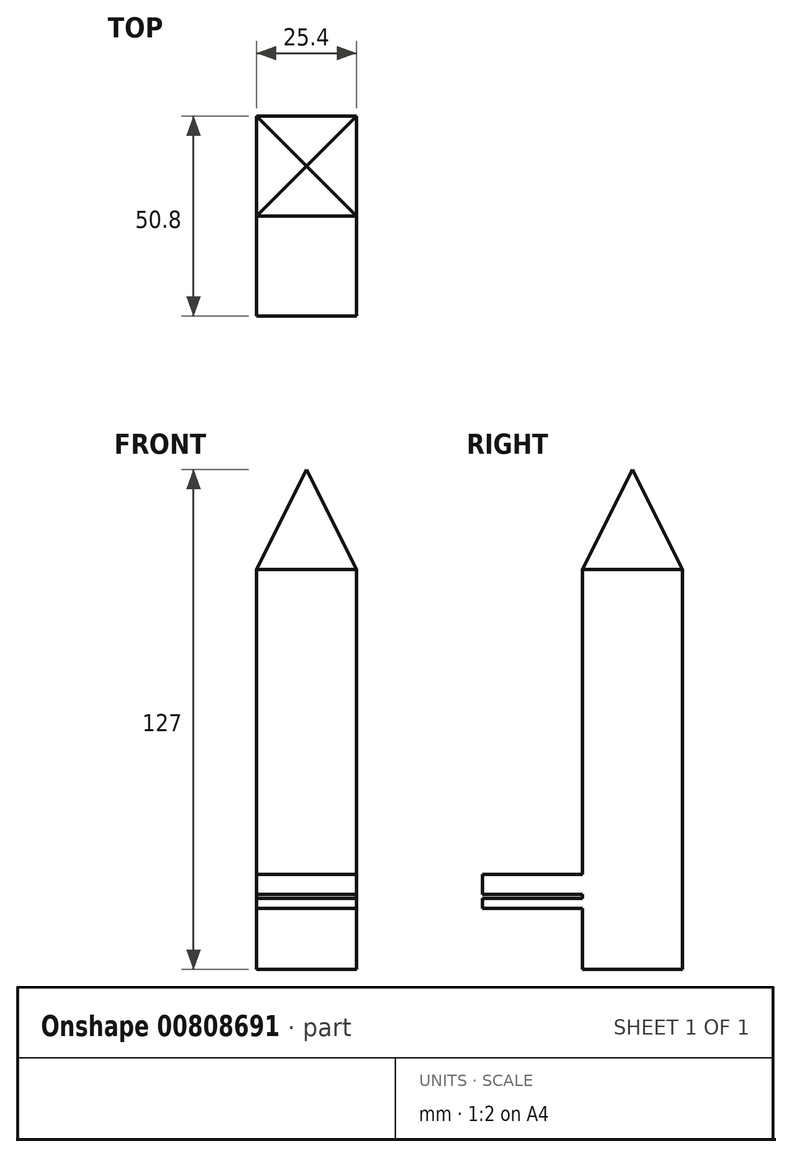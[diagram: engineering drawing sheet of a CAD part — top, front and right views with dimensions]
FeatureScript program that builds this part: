
annotation { "Feature Type Name" : "Feature", "Feature Type Description" : "" }
export const myFeature = defineFeature(function(context is Context, id is Id, definition is map)
    precondition{}
    {
        {
            var Q0;
            Q0=qCreatedBy(makeId("Top.planeOp"),FACE);
            var sketch = newSketch(context, id + "F0", { "sketchPlane" : qUnion([Q0])});
            skLineSegment(sketch, "E0.bottom", {"start": v(-11.7, 11.54) * mm, "end": v(13.7, 11.54) * mm});
            skLineSegment(sketch, "E0.top", {"start": v(-11.7, -13.86) * mm, "end": v(13.7, -13.86) * mm});
            skLineSegment(sketch, "E0.left", {"start": v(-11.7, 11.54) * mm, "end": v(-11.7, -13.86) * mm});
            skLineSegment(sketch, "E0.right", {"start": v(13.7, 11.54) * mm, "end": v(13.7, -13.86) * mm});
            skSolve(sketch);
        }
        {
            var Q0;
            Q0 = qSketchRegion(id + "F0", true);
            extrude(context, id + "F1", {"entities" : qUnion([Q0]), "depth" : 101.6 * mm, "offsetDistance" : 25.4 * mm});
        }
        {
            var Q0;
            Q0=makeQuery(id+"F1.opExtrude","CAP_FACE",FACE,{"disambiguationData":[OSD([sQuery(id+"F0.wireOp",EDGE,"E0.bottom"),sQuery(id+"F0.wireOp",EDGE,"E0.top"),sQuery(id+"F0.wireOp",EDGE,"E0.left"),sQuery(id+"F0.wireOp",EDGE,"E0.right")])],"isStart":false});
            cPlane(context, id + "F2", {"entities" : qUnion([Q0]), "cplaneType" : CPlaneType.OFFSET, "offset" : 25.4 * mm, "width" : 152.4 * mm, "height" : 152.4 * mm});
        }
        {
            var Q0;
            Q0=qCreatedBy(id+"F2.planeOp",FACE);
            var sketch = newSketch(context, id + "F3", { "sketchPlane" : qUnion([Q0])});
            skLineSegment(sketch, "E1.bottom", {"start": v(-11.7, 11.54) * mm, "end": v(13.7, 11.54) * mm, "construction": true});
            skLineSegment(sketch, "E1.top", {"start": v(-11.7, -13.86) * mm, "end": v(13.7, -13.86) * mm, "construction": true});
            skLineSegment(sketch, "E1.left", {"start": v(-11.7, 11.54) * mm, "end": v(-11.7, -13.86) * mm, "construction": true});
            skLineSegment(sketch, "E1.right", {"start": v(13.7, 11.54) * mm, "end": v(13.7, -13.86) * mm, "construction": true});
            skLineSegment(sketch, "E2", {"start": v(1, -13.86) * mm, "end": v(1, 11.54) * mm, "construction": true});
            skLineSegment(sketch, "E3", {"start": v(-11.7, -1.16) * mm, "end": v(13.7, -1.16) * mm, "construction": true});
            skPoint(sketch, "E4", {"position": v(1, -1.16) * mm});
            skSolve(sketch);
        }
        {
            var Q0;
            Q0=sQuery(id+"F3.wireOp",VERTEX,"E4");
            var Q1;
            Q1=makeQuery(id+"F1.opExtrude","CAP_FACE",FACE,{"disambiguationData":[OSD([sQuery(id+"F0.wireOp",EDGE,"E0.bottom"),sQuery(id+"F0.wireOp",EDGE,"E0.top"),sQuery(id+"F0.wireOp",EDGE,"E0.left"),sQuery(id+"F0.wireOp",EDGE,"E0.right")])],"isStart":false});
            loft(context, id + "F4", {"sheetProfilesArray" : [{ "sheetProfileEntities" : qUnion([Q0]) }, { "sheetProfileEntities" : qUnion([Q1]) }]});
        }
        {
            var Q0;
            Q0=makeQuery(id+"F1.opExtrude","SWEPT_FACE",FACE,{"disambiguationData":[OSD([sQuery(id+"F0.wireOp",EDGE,"E0.top")])]});
            var sketch = newSketch(context, id + "F5", { "sketchPlane" : qUnion([Q0])});
            skLineSegment(sketch, "E5.bottom", {"start": v(13.7, 19.05) * mm, "end": v(-11.7, 19.05) * mm});
            skLineSegment(sketch, "E5.top", {"start": v(13.7, 24.13) * mm, "end": v(-11.7, 24.13) * mm});
            skLineSegment(sketch, "E5.left", {"start": v(13.7, 19.05) * mm, "end": v(13.7, 24.13) * mm});
            skLineSegment(sketch, "E5.right", {"start": v(-11.7, 19.05) * mm, "end": v(-11.7, 24.13) * mm});
            skSolve(sketch);
        }
        {
            var Q0;
            {var subQ0=sQuery(id+"F5.wireOp",EDGE,"E5.bottom");Q0=makeQuery(id+"F5.imprint","IMPRINT",FACE,{"disambiguationData":[TD([[makeQuery(id+"F5.imprint","IMPRINT",EDGE,{"derivedFrom":subQ0}),1.0]])]});}
            var sketch = newSketch(context, id + "F6", { "sketchPlane" : qUnion([Q0])});
            skLineSegment(sketch, "E6.bottom", {"start": v(13.7, 15.5) * mm, "end": v(-11.7, 15.5) * mm});
            skLineSegment(sketch, "E6.top", {"start": v(13.7, 18.03) * mm, "end": v(-11.7, 18.03) * mm});
            skLineSegment(sketch, "E6.left", {"start": v(13.7, 15.5) * mm, "end": v(13.7, 18.03) * mm});
            skLineSegment(sketch, "E6.right", {"start": v(-11.7, 15.5) * mm, "end": v(-11.7, 18.03) * mm});
            skSolve(sketch);
        }
        {
            var Q0;
            Q0 = qSketchRegion(id + "F5", true);
            extrude(context, id + "F7", {"entities" : qUnion([Q0]), "operationType" : NewBodyOperationType.ADD, "depth" : 25.4 * mm, "offsetDistance" : 25.4 * mm});
        }
        {
            var Q0;
            Q0 = qSketchRegion(id + "F6", true);
            extrude(context, id + "F8", {"entities" : qUnion([Q0]), "operationType" : NewBodyOperationType.ADD, "depth" : 25.4 * mm, "offsetDistance" : 25.4 * mm});
        }
    });
